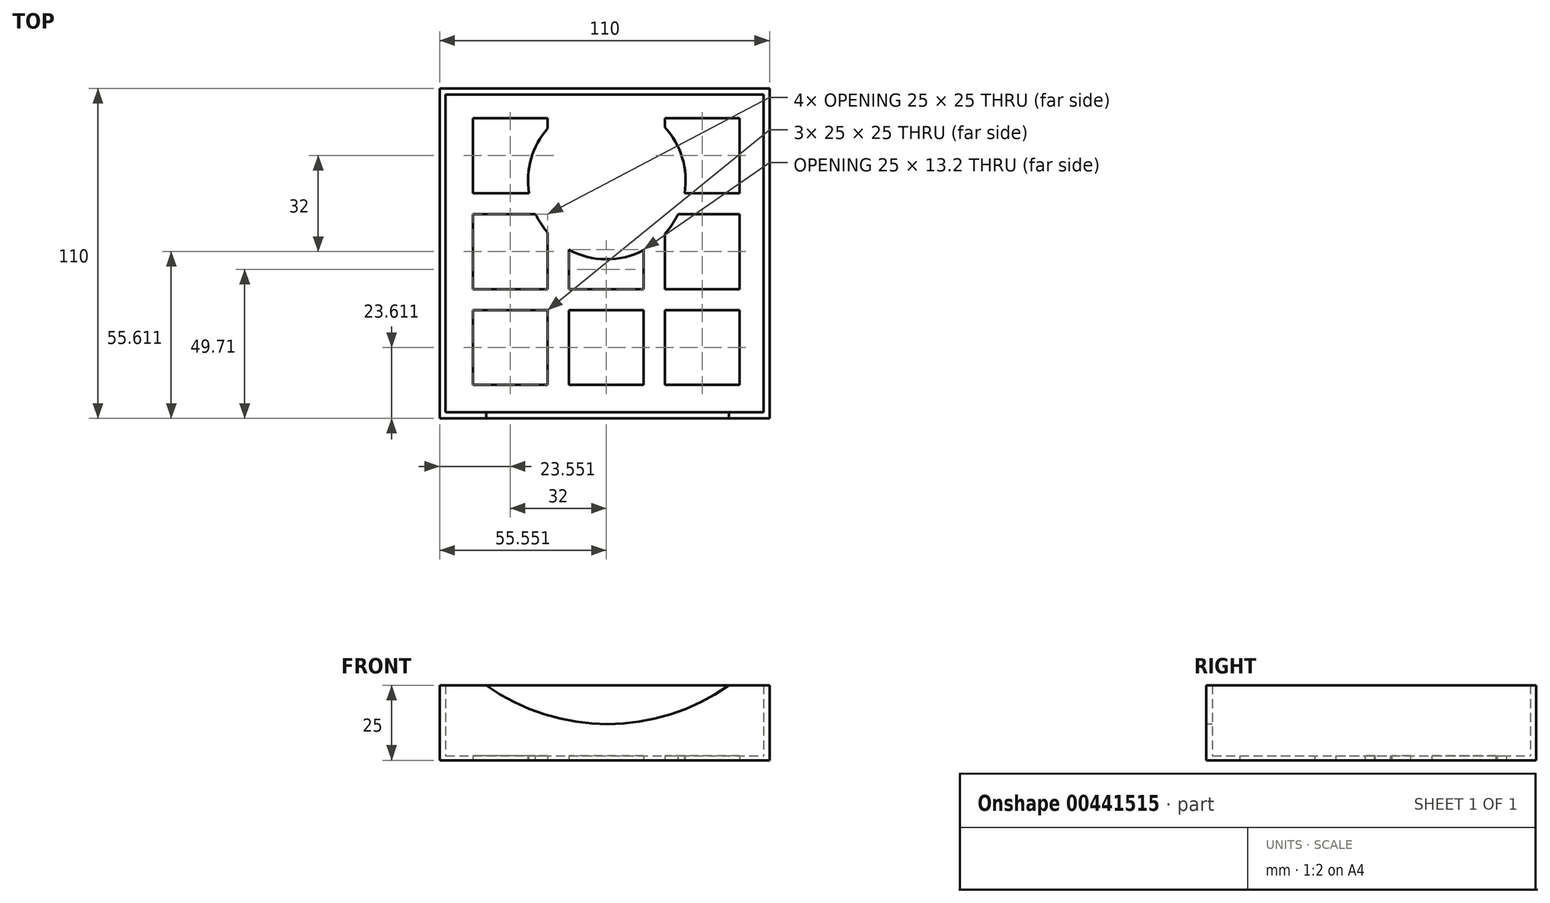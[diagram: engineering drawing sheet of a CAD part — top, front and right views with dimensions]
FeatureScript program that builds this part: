
annotation { "Feature Type Name" : "Feature", "Feature Type Description" : "" }
export const myFeature = defineFeature(function(context is Context, id is Id, definition is map)
    precondition{}
    {
        {
            var Q0;
            Q0=qCreatedBy(makeId("Top.planeOp"),FACE);
            var sketch = newSketch(context, id + "F0", { "sketchPlane" : qUnion([Q0])});
            skLineSegment(sketch, "E0.bottom", {"start": v(0, 0) * mm, "end": v(110, 0) * mm});
            skLineSegment(sketch, "E0.top", {"start": v(0, 110) * mm, "end": v(110, 110) * mm});
            skLineSegment(sketch, "E0.left", {"start": v(0, 0) * mm, "end": v(0, 110) * mm});
            skLineSegment(sketch, "E0.right", {"start": v(110, 0) * mm, "end": v(110, 110) * mm});
            skLineSegment(sketch, "E1.0", {"start": v(2, 108) * mm, "end": v(108, 108) * mm});
            skLineSegment(sketch, "E1.1", {"start": v(2, 2) * mm, "end": v(2, 108) * mm});
            skLineSegment(sketch, "E1.2", {"start": v(2, 2) * mm, "end": v(108, 2) * mm});
            skLineSegment(sketch, "E1.3", {"start": v(108, 2) * mm, "end": v(108, 108) * mm});
            skSolve(sketch);
        }
        {
            var Q0;
            Q0 = qSketchRegion(id + "F0", true);
            extrude(context, id + "F1", {"entities" : qUnion([Q0]), "depth" : 25 * mm});
        }
        {
            var Q0;
            Q0=qCreatedBy(makeId("Top.planeOp"),FACE);
            var sketch = newSketch(context, id + "F2", { "sketchPlane" : qUnion([Q0])});
            skLineSegment(sketch, "E2.0", {"start": v(2, 2) * mm, "end": v(2, 108) * mm});
            skLineSegment(sketch, "E2.1", {"start": v(2, 108) * mm, "end": v(108, 108) * mm});
            skLineSegment(sketch, "E2.2", {"start": v(108, 2) * mm, "end": v(108, 108) * mm});
            skLineSegment(sketch, "E2.3", {"start": v(2, 2) * mm, "end": v(108, 2) * mm});
            skSolve(sketch);
        }
        {
            var Q0;
            Q0 = qSketchRegion(id + "F2", true);
            extrude(context, id + "F3", {"entities" : qUnion([Q0]), "operationType" : NewBodyOperationType.ADD, "depth" : 1.5 * mm});
        }
        {
            var Q0;
            Q0=qCreatedBy(makeId("Top.planeOp"),FACE);
            var sketch = newSketch(context, id + "F4", { "sketchPlane" : qUnion([Q0])});
            skLineSegment(sketch, "E3.bottom", {"start": v(11.05, 100.11) * mm, "end": v(36.05, 100.11) * mm});
            skLineSegment(sketch, "E3.top", {"start": v(11.05, 75.11) * mm, "end": v(36.05, 75.11) * mm});
            skLineSegment(sketch, "E3.left", {"start": v(11.05, 100.11) * mm, "end": v(11.05, 75.11) * mm});
            skLineSegment(sketch, "E3.right", {"start": v(36.05, 100.11) * mm, "end": v(36.05, 75.11) * mm});
            skLineSegment(sketch, "E4.0.1.0", {"start": v(11.05, 68.11) * mm, "end": v(36.05, 68.11) * mm});
            skLineSegment(sketch, "E4.0.1.1", {"start": v(11.05, 43.11) * mm, "end": v(36.05, 43.11) * mm});
            skLineSegment(sketch, "E4.0.1.2", {"start": v(11.05, 68.11) * mm, "end": v(11.05, 43.11) * mm});
            skLineSegment(sketch, "E4.0.1.3", {"start": v(36.05, 68.11) * mm, "end": v(36.05, 43.11) * mm});
            skLineSegment(sketch, "E4.0.2.0", {"start": v(11.05, 36.11) * mm, "end": v(36.05, 36.11) * mm});
            skLineSegment(sketch, "E4.0.2.1", {"start": v(11.05, 11.11) * mm, "end": v(36.05, 11.11) * mm});
            skLineSegment(sketch, "E4.0.2.2", {"start": v(11.05, 36.11) * mm, "end": v(11.05, 11.11) * mm});
            skLineSegment(sketch, "E4.0.2.3", {"start": v(36.05, 36.11) * mm, "end": v(36.05, 11.11) * mm});
            skLineSegment(sketch, "E4.1.0.0", {"start": v(43.05, 100.11) * mm, "end": v(68.05, 100.11) * mm});
            skLineSegment(sketch, "E4.1.0.1", {"start": v(43.05, 75.11) * mm, "end": v(68.05, 75.11) * mm});
            skLineSegment(sketch, "E4.1.0.2", {"start": v(43.05, 100.11) * mm, "end": v(43.05, 75.11) * mm});
            skLineSegment(sketch, "E4.1.0.3", {"start": v(68.05, 100.11) * mm, "end": v(68.05, 75.11) * mm});
            skLineSegment(sketch, "E4.1.1.0", {"start": v(43.05, 68.11) * mm, "end": v(68.05, 68.11) * mm});
            skLineSegment(sketch, "E4.1.1.1", {"start": v(43.05, 43.11) * mm, "end": v(68.05, 43.11) * mm});
            skLineSegment(sketch, "E4.1.1.2", {"start": v(43.05, 68.11) * mm, "end": v(43.05, 43.11) * mm});
            skLineSegment(sketch, "E4.1.1.3", {"start": v(68.05, 68.11) * mm, "end": v(68.05, 43.11) * mm});
            skLineSegment(sketch, "E4.1.2.0", {"start": v(43.05, 36.11) * mm, "end": v(68.05, 36.11) * mm});
            skLineSegment(sketch, "E4.1.2.1", {"start": v(43.05, 11.11) * mm, "end": v(68.05, 11.11) * mm});
            skLineSegment(sketch, "E4.1.2.2", {"start": v(43.05, 36.11) * mm, "end": v(43.05, 11.11) * mm});
            skLineSegment(sketch, "E4.1.2.3", {"start": v(68.05, 36.11) * mm, "end": v(68.05, 11.11) * mm});
            skLineSegment(sketch, "E4.2.0.0", {"start": v(75.05, 100.11) * mm, "end": v(100.05, 100.11) * mm});
            skLineSegment(sketch, "E4.2.0.1", {"start": v(75.05, 75.11) * mm, "end": v(100.05, 75.11) * mm});
            skLineSegment(sketch, "E4.2.0.2", {"start": v(75.05, 100.11) * mm, "end": v(75.05, 75.11) * mm});
            skLineSegment(sketch, "E4.2.0.3", {"start": v(100.05, 100.11) * mm, "end": v(100.05, 75.11) * mm});
            skLineSegment(sketch, "E4.2.1.0", {"start": v(75.05, 68.11) * mm, "end": v(100.05, 68.11) * mm});
            skLineSegment(sketch, "E4.2.1.1", {"start": v(75.05, 43.11) * mm, "end": v(100.05, 43.11) * mm});
            skLineSegment(sketch, "E4.2.1.2", {"start": v(75.05, 68.11) * mm, "end": v(75.05, 43.11) * mm});
            skLineSegment(sketch, "E4.2.1.3", {"start": v(100.05, 68.11) * mm, "end": v(100.05, 43.11) * mm});
            skLineSegment(sketch, "E4.2.2.0", {"start": v(75.05, 36.11) * mm, "end": v(100.05, 36.11) * mm});
            skLineSegment(sketch, "E4.2.2.1", {"start": v(75.05, 11.11) * mm, "end": v(100.05, 11.11) * mm});
            skLineSegment(sketch, "E4.2.2.2", {"start": v(75.05, 36.11) * mm, "end": v(75.05, 11.11) * mm});
            skLineSegment(sketch, "E4.2.2.3", {"start": v(100.05, 36.11) * mm, "end": v(100.05, 11.11) * mm});
            skLineSegment(sketch, "E4.direction1", {"start": v(11.05, 75.11) * mm, "end": v(43.05, 75.11) * mm, "construction": true});
            skLineSegment(sketch, "E4.direction2", {"start": v(11.05, 75.11) * mm, "end": v(11.05, 43.11) * mm, "construction": true});
            skSolve(sketch);
        }
        {
            var Q0;
            Q0 = qSketchRegion(id + "F4", true);
            extrude(context, id + "F5", {"entities" : qUnion([Q0]), "operationType" : NewBodyOperationType.REMOVE, "depth" : 25 * mm});
        }
        {
            var Q0;
            Q0=makeQuery(id+"F3.opExtrude","CAP_FACE",FACE,{"disambiguationData":[OSD([sQuery(id+"F2.wireOp",EDGE,"E2.0"),sQuery(id+"F2.wireOp",EDGE,"E2.1"),sQuery(id+"F2.wireOp",EDGE,"E2.2"),sQuery(id+"F2.wireOp",EDGE,"E2.3")])],"isStart":false});
            var sketch = newSketch(context, id + "F6", { "sketchPlane" : qUnion([Q0])});
            skCircle(sketch, "E5", {"center": v(55.74, 79.3) * mm, "radius": 26.26 * mm});
            skSolve(sketch);
        }
        {
            var Q0;
            Q0 = qSketchRegion(id + "F6", true);
            var Q1;
            Q1=makeQuery(id+"F3.boolean.opBoolean","MERGE",FACE,{"derivedFrom":[makeQuery(id+"F1.opExtrude","CAP_FACE",FACE,{"disambiguationData":[OSD([sQuery(id+"F0.wireOp",EDGE,"E0.bottom"),sQuery(id+"F0.wireOp",EDGE,"E0.top"),sQuery(id+"F0.wireOp",EDGE,"E0.left"),sQuery(id+"F0.wireOp",EDGE,"E0.right"),sQuery(id+"F0.wireOp",EDGE,"E1.0"),sQuery(id+"F0.wireOp",EDGE,"E1.1"),sQuery(id+"F0.wireOp",EDGE,"E1.2"),sQuery(id+"F0.wireOp",EDGE,"E1.3")])],"isStart":true}),makeQuery(id+"F3.opExtrude","CAP_FACE",FACE,{"disambiguationData":[OSD([sQuery(id+"F2.wireOp",EDGE,"E2.0"),sQuery(id+"F2.wireOp",EDGE,"E2.1"),sQuery(id+"F2.wireOp",EDGE,"E2.2"),sQuery(id+"F2.wireOp",EDGE,"E2.3")])],"isStart":true})]});
            extrude(context, id + "F7", {"entities" : qUnion([Q0]), "operationType" : NewBodyOperationType.ADD, "endBound" : BoundingType.UP_TO_SURFACE, "oppositeDirection" : true, "endBoundEntityFace" : qUnion([Q1]), "depth" : 25 * mm});
        }
        {
            var Q0;
            Q0=makeQuery(id+"F1.opExtrude","SWEPT_FACE",FACE,{"disambiguationData":[OSD([sQuery(id+"F0.wireOp",EDGE,"E0.bottom")])]});
            var sketch = newSketch(context, id + "F8", { "sketchPlane" : qUnion([Q0])});
            skArc(sketch, "E6", {"start": v(10.87, 28.62) * mm, "mid": v(55.86, 12.06) * mm, "end": v(100.91, 28.47) * mm});
            skLineSegment(sketch, "E7", {"start": v(10.87, 28.62) * mm, "end": v(100.91, 28.47) * mm});
            skSolve(sketch);
        }
        {
            var Q0;
            Q0 = qSketchRegion(id + "F8", true);
            extrude(context, id + "F9", {"entities" : qUnion([Q0]), "operationType" : NewBodyOperationType.REMOVE, "oppositeDirection" : true, "depth" : 25 * mm});
        }
    });
